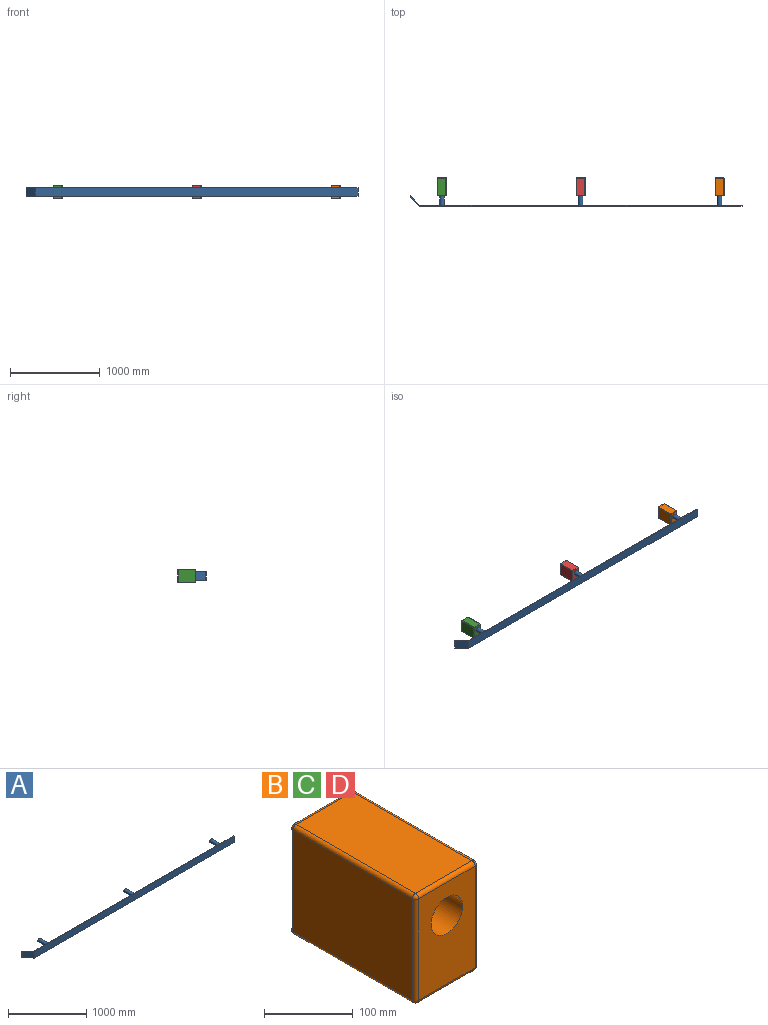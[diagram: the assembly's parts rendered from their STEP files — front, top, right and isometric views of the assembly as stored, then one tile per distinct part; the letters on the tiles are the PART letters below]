
ASSEMBLY  parts=4 mates=5
PART A: 14 faces, bbox 3705x160x100 mm
  f0: plane 3705x115mm, normal (0,0,-1), area 36630mm2, adj f1,f3,f4,f11,f12,f13
  f1: plane 3600x100mm, normal (0,1,0), area 354109.5mm2, adj f0,f2,f4,f5,f7,f9,f11
  f2: plane 3705x115mm, normal (0,0,1), area 36630mm2, adj f1,f3,f4,f11,f12,f13
  f3: plane 3600x100mm, normal (0,-1,0), area 360000mm2, adj f0,f2,f4,f13
  f4: plane 100x10mm, normal (1,0,0), area 1000mm2, adj f0,f1,f2,f3
  f5: cylinder r=25mm len=150mm, axis (0,-1,0), area 23561.9mm2, adj f1,f6
  f6: plane 50x50mm, normal (0,1,0), area 1963.5mm2, adj f5
  f7: cylinder r=25mm len=150mm, axis (0,-1,0), area 23561.9mm2, adj f1,f8
  f8: plane 50x50mm, normal (0,1,0), area 1963.5mm2, adj f7
  f9: cylinder r=25mm len=150mm, axis (0,-1,0), area 23561.9mm2, adj f1,f10
  f10: plane 50x50mm, normal (0,1,0), area 1963.5mm2, adj f9
  f11: plane 105x105mm, normal (0.71,0.71,0), area 14849.2mm2, adj f0,f1,f2,f12
  f12: plane 100x2mm, normal (-1,0,0), area 200mm2, adj f0,f2,f11,f13
  f13: plane 113x105mm, normal (-0.73,-0.68,0), area 15425.3mm2, adj f0,f2,f3,f12
PART B: 28 faces, bbox 100x200x150 mm
  f0: plane 190x90mm, normal (0,0,1), area 17100mm2, adj f16,f21,f24,f27
  f1: plane 190x140mm, normal (-1,0,0), area 26600mm2, adj f13,f22,f23,f27
  f2: plane 190x90mm, normal (0,0,-1), area 17100mm2, adj f8,f12,f13,f14
  f3: plane 190x140mm, normal (1,0,0), area 26600mm2, adj f8,f11,f15,f16
  f4: plane 140x90mm, normal (0,-1,0), area 10636.5mm2, adj f6,f11,f12,f21,f22
  f5: plane 140x90mm, normal (0,1,0), area 12600mm2, adj f14,f15,f23,f24
  f6: cylinder r=25mm len=150mm, axis (0,-1,0), area 23561.9mm2, adj f4,f7
  f7: plane 50x50mm, normal (0,-1,0), area 1963.5mm2, adj f6
  f8: cylinder r=5mm len=190mm, axis (0,1,0), area 1492.3mm2, adj f2,f3,f9,f10
  f9: sphere r=5mm, area 39.3mm2, adj f8,f11,f12
  f10: sphere r=5mm, area 39.3mm2, adj f8,f14,f15
  f11: cylinder r=5mm len=140mm, axis (0,0,-1), area 1099.6mm2, adj f3,f4,f9,f17
  f12: cylinder r=5mm len=90mm, axis (-1,0,0), area 706.9mm2, adj f2,f4,f9,f18
  f13: cylinder r=5mm len=190mm, axis (0,-1,0), area 1492.3mm2, adj f1,f2,f18,f19
  f14: cylinder r=5mm len=90mm, axis (1,0,0), area 706.9mm2, adj f2,f5,f10,f19
  f15: cylinder r=5mm len=140mm, axis (0,0,1), area 1099.6mm2, adj f3,f5,f10,f20
  f16: cylinder r=5mm len=190mm, axis (0,-1,0), area 1492.3mm2, adj f0,f3,f17,f20
  f17: sphere r=5mm, area 39.3mm2, adj f11,f16,f21
  f18: sphere r=5mm, area 39.3mm2, adj f12,f13,f22
  f19: sphere r=5mm, area 39.3mm2, adj f13,f14,f23
  f20: sphere r=5mm, area 39.3mm2, adj f15,f16,f24
  f21: cylinder r=5mm len=90mm, axis (1,0,0), area 706.9mm2, adj f0,f4,f17,f25
  f22: cylinder r=5mm len=140mm, axis (0,0,1), area 1099.6mm2, adj f1,f4,f18,f25
  f23: cylinder r=5mm len=140mm, axis (0,0,-1), area 1099.6mm2, adj f1,f5,f19,f26
  f24: cylinder r=5mm len=90mm, axis (-1,0,0), area 706.9mm2, adj f0,f5,f20,f26
  f25: sphere r=5mm, area 39.3mm2, adj f21,f22,f27
  f26: sphere r=5mm, area 39.3mm2, adj f23,f24,f27
  f27: cylinder r=5mm len=190mm, axis (0,1,0), area 1492.3mm2, adj f0,f1,f25,f26
PART C: same geometry as B
PART D: same geometry as B
PLACE A t=(-2745.7,432.95,-70.75)mm
PLACE B t=(546.65,737.95,-95.75)mm fixed
PLACE C t=(-2553.35,737.95,-95.75)mm
PLACE D t=(-1003.35,737.95,-95.75)mm
MATE planar C.f5 <-> B.f5  axis (0,1,0) through (-2495.7,737.95,-20.75)mm
MATE cylindrical A.f5 <-> B.f6  axis (0,-1,0) through (604.3,432.95,4.25)mm
MATE cylindrical A.f7 <-> C.f6  axis (0,1,0) through (-2495.7,432.95,4.25)mm
MATE planar D.f5 <-> C.f5  axis (0,1,0) through (-945.7,737.95,-20.75)mm
MATE cylindrical D.f6 <-> A.f9  axis (0,-1,0) through (-945.7,537.95,4.25)mm
